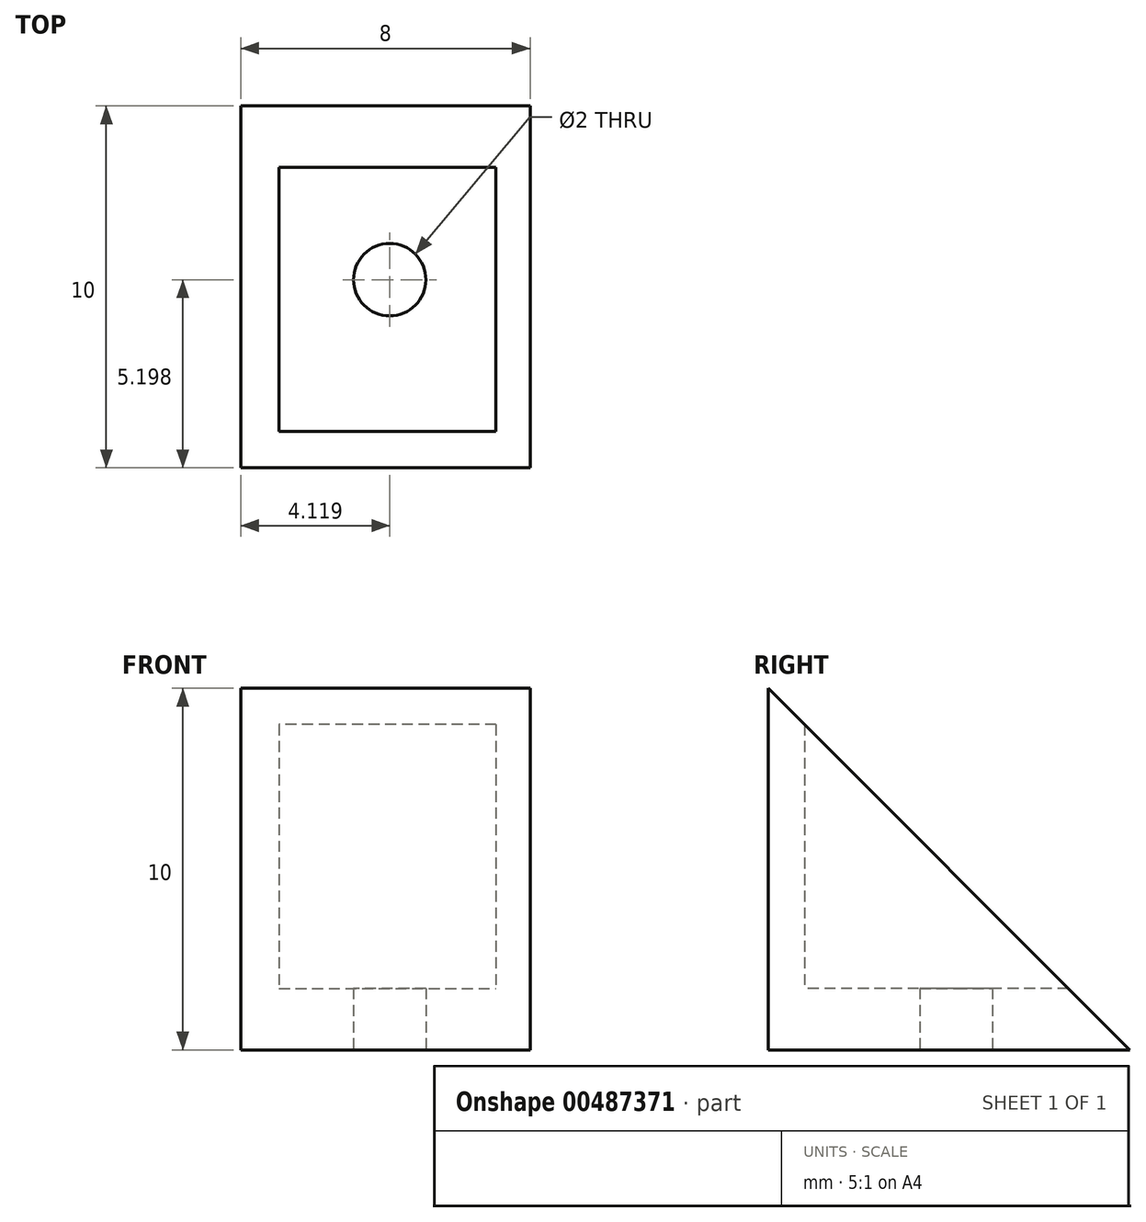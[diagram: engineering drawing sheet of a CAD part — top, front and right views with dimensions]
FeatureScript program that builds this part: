
annotation { "Feature Type Name" : "Feature", "Feature Type Description" : "" }
export const myFeature = defineFeature(function(context is Context, id is Id, definition is map)
    precondition{}
    {
        {
            var Q0;
            Q0=qCreatedBy(makeId("Right.planeOp"),FACE);
            var sketch = newSketch(context, id + "F0", { "sketchPlane" : qUnion([Q0])});
            skLineSegment(sketch, "E0", {"start": v(0, 0) * mm, "end": v(0, 10) * mm});
            skLineSegment(sketch, "E1", {"start": v(0, 10) * mm, "end": v(10, 0) * mm});
            skLineSegment(sketch, "E2", {"start": v(10, 0) * mm, "end": v(0, 0) * mm});
            skSolve(sketch);
        }
        {
            var Q0;
            Q0 = qSketchRegion(id + "F0", true);
            extrude(context, id + "F1", {"entities" : qUnion([Q0]), "depth" : 8 * mm});
        }
        {
            var Q0;
            Q0=qCreatedBy(makeId("Top.planeOp"),FACE);
            var sketch = newSketch(context, id + "F2", { "sketchPlane" : qUnion([Q0])});
            skLineSegment(sketch, "E3.bottom", {"start": v(1.06, 10) * mm, "end": v(7.06, 10) * mm});
            skLineSegment(sketch, "E3.top", {"start": v(1.06, 1) * mm, "end": v(7.06, 1) * mm});
            skLineSegment(sketch, "E3.left", {"start": v(1.06, 10) * mm, "end": v(1.06, 1) * mm});
            skLineSegment(sketch, "E3.right", {"start": v(7.06, 10) * mm, "end": v(7.06, 1) * mm});
            skSolve(sketch);
        }
        {
            var Q0;
            Q0 = qSketchRegion(id + "F2", true);
            extrude(context, id + "F3", {"entities" : qUnion([Q0]), "operationType" : NewBodyOperationType.REMOVE, "depth" : 22.4 * mm, "hasSecondDirection" : true, "secondDirectionOppositeDirection" : false, "secondDirectionDepth" : 1.7 * mm});
        }
        {
            var Q0;
            Q0=qCreatedBy(makeId("Top.planeOp"),FACE);
            var sketch = newSketch(context, id + "F4", { "sketchPlane" : qUnion([Q0])});
            skCircle(sketch, "E4", {"center": v(4.12, 5.2) * mm, "radius": 1 * mm});
            skSolve(sketch);
        }
        {
            var Q0;
            Q0 = qSketchRegion(id + "F4", true);
            extrude(context, id + "F5", {"entities" : qUnion([Q0]), "operationType" : NewBodyOperationType.REMOVE, "depth" : 19.8 * mm});
        }
    });
